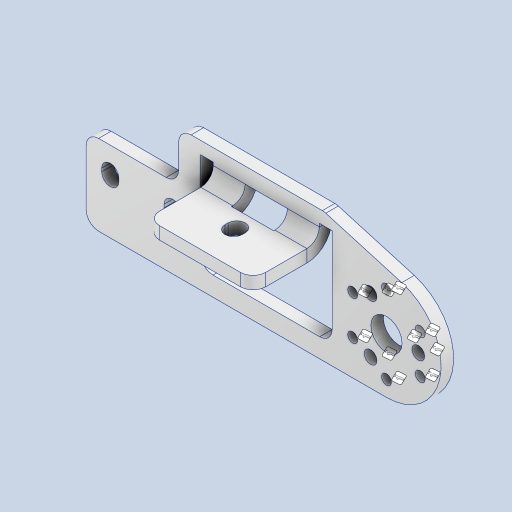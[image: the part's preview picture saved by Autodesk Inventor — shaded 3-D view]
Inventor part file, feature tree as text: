
AUTODESK INVENTOR PART (.ipt)
format: ipt  version: 2023 (Build 270158000, 158)  size: 313,856 bytes
history: native  units: mm
features: other x3, sketch x3, fillet x1, hole x1
ambient origin geometry x8: Origin, YZ Plane, XZ Plane, XY Plane, X Axis, Y Axis, Z Axis, Center Point
bodies: Body1 (feature_tree)
feature tree (8):
  other  "ソリッド1"
  other  "折り曲げ4"
  fillet  "フィレット1"  Radius=35.0mm
  hole  "穴1"  [1 undecoded]
  sketch  "スケッチ1"
  other  "プレート1"
  sketch  "スケッチ5"
  sketch  "スケッチ6"
note: 1 required parameter value undecoded (feature->parameter linkage not recoverable at this tier; creation-order binding heuristic only, values carry confidence <= 0.55)
